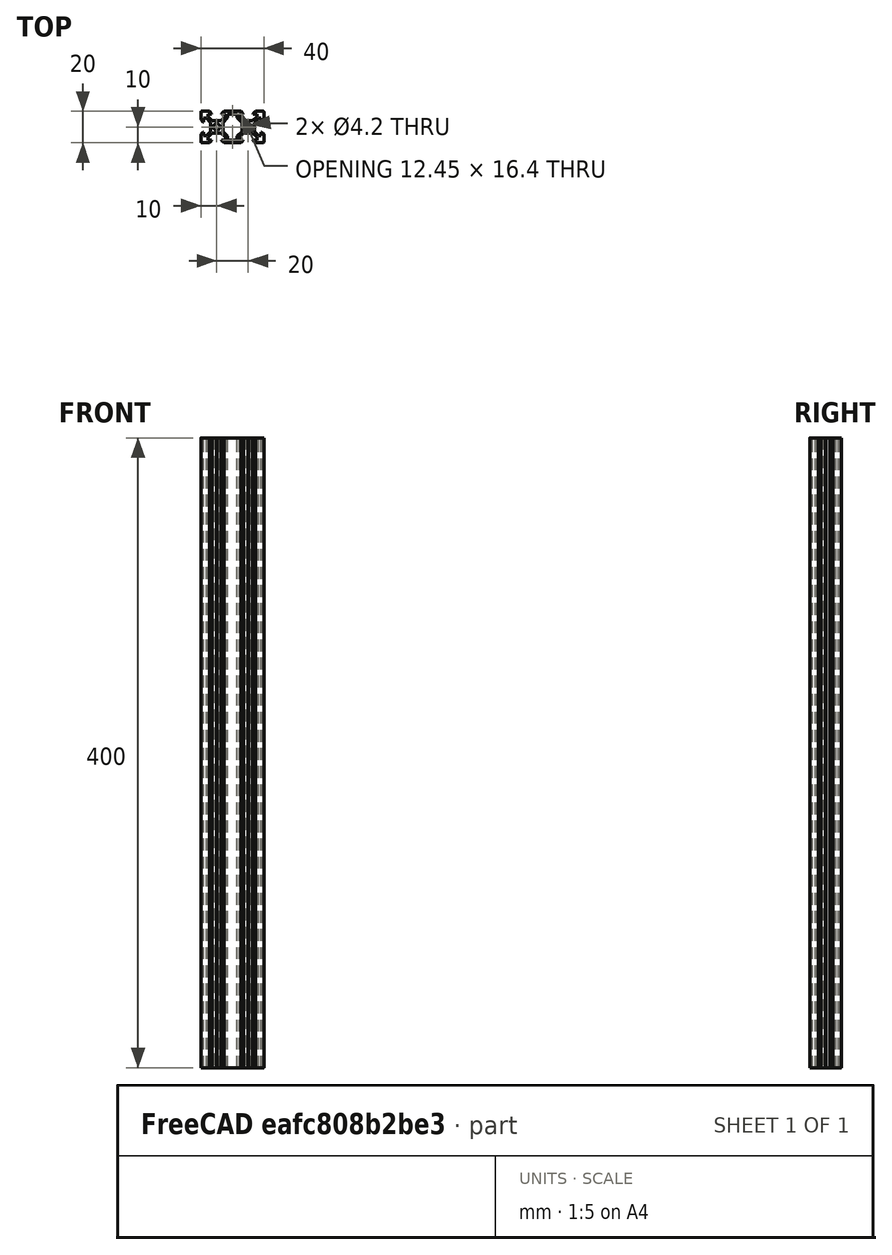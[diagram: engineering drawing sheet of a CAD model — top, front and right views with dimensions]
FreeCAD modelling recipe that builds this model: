
FCSTD DOCUMENT  (FreeCAD 0.20R25566 (Git))
Label: 2040-400
License: All rights reserved
LicenseURL: http://en.wikipedia.org/wiki/All_rights_reserved
objects: Sketcher::SketchObject×1, PartDesign::Pad×1, PartDesign::Body×1
note: 4 computed .brp shape members not serialized (recipe doc carries the construction recipe); baked Part::Feature solids carry a one-line shape summary decoded from their .brp

FEATURE [Sketcher::SketchObject] Sketch
  FullyConstrained = true
  MapMode = 5
  Support = -> [XY_Plane]
  sketch-geometry (114):
    g0: LineSegment StartX=-10 StartY=4.58 StartZ=0 EndX=-10 EndY=9.5 EndZ=0
    g1: LineSegment StartX=-9.5 StartY=10 StartZ=0 EndX=-4.58 EndY=10 EndZ=0
    g2: LineSegment StartX=-5.5 StartY=8.2 StartZ=0 EndX=-3.125 EndY=8.2 EndZ=0
    g3: LineSegment StartX=-8.2 StartY=5.5 StartZ=0 EndX=-8.2 EndY=3.125 EndZ=0
    g4: LineSegment StartX=-0.125 StartY=3.9 StartZ=0 EndX=-2.83934 EndY=3.9 EndZ=0
    g5: LineSegment StartX=-3.9 StartY=2.83934 StartZ=0 EndX=-3.9 EndY=0.125 EndZ=0
    g6: ArcOfCircle CenterX=0 CenterY=3.9 CenterZ=0 NormalX=0 NormalY=0 NormalZ=1 AngleXU=0 Radius=0.125 StartAngle=3.14159 EndAngle=6.28319
    g7: ArcOfCircle CenterX=-3.9 CenterY=0 CenterZ=0 NormalX=0 NormalY=0 NormalZ=1 AngleXU=0 Radius=0.125 StartAngle=4.71239 EndAngle=7.85398
    g8: ArcOfCircle CenterX=-9.5 CenterY=9.5 CenterZ=0 NormalX=0 NormalY=0 NormalZ=1 AngleXU=0 Radius=0.5 StartAngle=1.5708 EndAngle=3.14159
    g9: LineSegment StartX=-5.5 StartY=8.2 StartZ=0 EndX=-5.5 EndY=6.56066 EndZ=0
    g10: LineSegment StartX=-8.2 StartY=5.5 StartZ=0 EndX=-6.56066 EndY=5.5 EndZ=0
    g11: LineSegment StartX=-4.58 StartY=10 StartZ=0 EndX=-3.125 EndY=8.545 EndZ=0
    g12: LineSegment StartX=-3.125 StartY=8.545 StartZ=0 EndX=-3.125 EndY=8.2 EndZ=0
    g13: LineSegment StartX=-10 StartY=4.58 StartZ=0 EndX=-8.545 EndY=3.125 EndZ=0
    g14: LineSegment StartX=-8.545 StartY=3.125 StartZ=0 EndX=-8.2 EndY=3.125 EndZ=0
    g15: LineSegment StartX=-5.5 StartY=6.56066 StartZ=0 EndX=-2.83934 EndY=3.9 EndZ=0
    g16: LineSegment StartX=-6.56066 StartY=5.5 StartZ=0 EndX=-3.9 EndY=2.83934 EndZ=0
    g17: Circle CenterX=0 CenterY=0 CenterZ=0 NormalX=0 NormalY=0 NormalZ=1 AngleXU=0 Radius=2.1
    g18: LineSegment StartX=0.125 StartY=3.9 StartZ=0 EndX=2.83934 EndY=3.9 EndZ=0
    g19: LineSegment StartX=2.83934 StartY=3.9 StartZ=0 EndX=5.5 EndY=6.56066 EndZ=0
    g20: LineSegment StartX=5.5 StartY=6.56066 StartZ=0 EndX=5.5 EndY=8.2 EndZ=0
    g21: LineSegment StartX=3.125 StartY=8.2 StartZ=0 EndX=3.125 EndY=8.545 EndZ=0
    g22: LineSegment StartX=5.5 StartY=8.2 StartZ=0 EndX=3.125 EndY=8.2 EndZ=0
    g23: LineSegment StartX=7 StartY=5.93934 StartZ=0 EndX=3.9 EndY=2.83934 EndZ=0
    g24: LineSegment StartX=3.9 StartY=2.83934 StartZ=0 EndX=3.9 EndY=0.125 EndZ=0
    g25: ArcOfCircle CenterX=3.9 CenterY=0 CenterZ=0 NormalX=0 NormalY=0 NormalZ=1 AngleXU=0 Radius=0.125 StartAngle=1.5708 EndAngle=4.71239
    g26: LineSegment StartX=3.9 StartY=-0.125 StartZ=0 EndX=3.9 EndY=-2.83934 EndZ=0
    g27: LineSegment StartX=3.9 StartY=-2.83934 StartZ=0 EndX=7 EndY=-5.93934 EndZ=0
    g28: LineSegment StartX=4.58 StartY=-10 StartZ=0 EndX=3.125 EndY=-8.545 EndZ=0
    g29: LineSegment StartX=2.83934 StartY=-3.9 StartZ=0 EndX=5.5 EndY=-6.56066 EndZ=0
    g30: LineSegment StartX=3.125 StartY=-8.545 StartZ=0 EndX=3.125 EndY=-8.2 EndZ=0
    g31: LineSegment StartX=3.125 StartY=-8.2 StartZ=0 EndX=5.5 EndY=-8.2 EndZ=0
    g32: LineSegment StartX=5.5 StartY=-8.2 StartZ=0 EndX=5.5 EndY=-6.56066 EndZ=0
    g33: ArcOfCircle CenterX=0 CenterY=-3.9 CenterZ=0 NormalX=0 NormalY=0 NormalZ=1 AngleXU=0 Radius=0.125 StartAngle=0 EndAngle=3.14159
    g34: LineSegment StartX=0.125 StartY=-3.9 StartZ=0 EndX=2.83934 EndY=-3.9 EndZ=0
    g35: LineSegment StartX=-0.125 StartY=-3.9 StartZ=0 EndX=-2.83934 EndY=-3.9 EndZ=0
    g36: LineSegment StartX=-3.9 StartY=-0.125 StartZ=0 EndX=-3.9 EndY=-2.83934 EndZ=0
    g37: LineSegment StartX=-3.9 StartY=-2.83934 StartZ=0 EndX=-6.56066 EndY=-5.5 EndZ=0
    g38: LineSegment StartX=-6.56066 StartY=-5.5 StartZ=0 EndX=-8.2 EndY=-5.5 EndZ=0
    g39: LineSegment StartX=-8.2 StartY=-5.5 StartZ=0 EndX=-8.2 EndY=-3.125 EndZ=0
    g40: LineSegment StartX=-8.2 StartY=-3.125 StartZ=0 EndX=-8.545 EndY=-3.125 EndZ=0
    g41: LineSegment StartX=-8.545 StartY=-3.125 StartZ=0 EndX=-10 EndY=-4.58 EndZ=0
    g42: LineSegment StartX=-10 StartY=-4.58 StartZ=0 EndX=-10 EndY=-9.5 EndZ=0
    g43: ArcOfCircle CenterX=-9.5 CenterY=-9.5 CenterZ=0 NormalX=0 NormalY=0 NormalZ=1 AngleXU=0 Radius=0.5 StartAngle=3.14159 EndAngle=4.71239
    g44: LineSegment StartX=-9.5 StartY=-10 StartZ=0 EndX=-4.58 EndY=-10 EndZ=0
    g45: LineSegment StartX=-4.58 StartY=-10 StartZ=0 EndX=-3.125 EndY=-8.545 EndZ=0
    g46: LineSegment StartX=-2.83934 StartY=-3.9 StartZ=0 EndX=-5.5 EndY=-6.56066 EndZ=0
    g47: LineSegment StartX=-5.5 StartY=-6.56066 StartZ=0 EndX=-5.5 EndY=-8.2 EndZ=0
    g48: LineSegment StartX=-5.5 StartY=-8.2 StartZ=0 EndX=-3.125 EndY=-8.2 EndZ=0
    g49: LineSegment StartX=-3.125 StartY=-8.545 StartZ=0 EndX=-3.125 EndY=-8.2 EndZ=0
    g50: LineSegment StartX=3.125 StartY=8.545 StartZ=0 EndX=4.58 EndY=10 EndZ=0
    g51: LineSegment StartX=-3.9 StartY=2.83934 StartZ=0 EndX=-2.83934 EndY=3.9 EndZ=0
    g52: LineSegment StartX=3.9 StartY=2.83934 StartZ=0 EndX=2.83934 EndY=3.9 EndZ=0
    g53: LineSegment StartX=4.58 StartY=10 StartZ=0 EndX=15.42 EndY=10 EndZ=0
    g54: LineSegment StartX=4.58 StartY=-10 StartZ=0 EndX=15.42 EndY=-10 EndZ=0
    g55: LineSegment StartX=7 StartY=5.93934 StartZ=0 EndX=7 EndY=8.2 EndZ=0
    g56: LineSegment StartX=5.5 StartY=8.2 StartZ=0 EndX=7 EndY=8.2 EndZ=0
    g57: LineSegment StartX=7 StartY=-5.93934 StartZ=0 EndX=7 EndY=-8.2 EndZ=0
    g58: LineSegment StartX=7 StartY=8.2 StartZ=0 EndX=13 EndY=8.2 EndZ=0
    g59: LineSegment StartX=15.42 StartY=10 StartZ=0 EndX=16.875 EndY=8.545 EndZ=0
    g60: LineSegment StartX=16.875 StartY=8.545 StartZ=0 EndX=16.875 EndY=8.2 EndZ=0
    g61: LineSegment StartX=16.875 StartY=8.2 StartZ=0 EndX=14.5 EndY=8.2 EndZ=0
    g62: LineSegment StartX=15.42 StartY=-10 StartZ=0 EndX=16.875 EndY=-8.545 EndZ=0
    g63: LineSegment StartX=16.875 StartY=-8.545 StartZ=0 EndX=16.875 EndY=-8.2 EndZ=0
    g64: LineSegment StartX=16.875 StartY=-8.2 StartZ=0 EndX=14.5 EndY=-8.2 EndZ=0
    g65: LineSegment StartX=7 StartY=-8.2 StartZ=0 EndX=13 EndY=-8.2 EndZ=0
    g66: LineSegment StartX=13 StartY=8.2 StartZ=0 EndX=14.5 EndY=8.2 EndZ=0
    g67: LineSegment StartX=13 StartY=8.2 StartZ=0 EndX=13 EndY=5.93934 EndZ=0
    g68: LineSegment StartX=13 StartY=-8.2 StartZ=0 EndX=13 EndY=-5.93934 EndZ=0
    g69: LineSegment StartX=14.5 StartY=8.2 StartZ=0 EndX=14.5 EndY=6.56066 EndZ=0
    g70: LineSegment StartX=14.5 StartY=-8.2 StartZ=0 EndX=14.5 EndY=-6.56066 EndZ=0
    g71: LineSegment StartX=13 StartY=5.93934 StartZ=0 EndX=16.1 EndY=2.83934 EndZ=0
    g72: LineSegment StartX=14.5 StartY=6.56066 StartZ=0 EndX=17.1607 EndY=3.9 EndZ=0
    g73: LineSegment StartX=13 StartY=-5.93934 StartZ=0 EndX=16.1 EndY=-2.83934 EndZ=0
    g74: LineSegment StartX=14.5 StartY=-6.56066 StartZ=0 EndX=17.1607 EndY=-3.9 EndZ=0
    g75: LineSegment StartX=16.1 StartY=2.83934 StartZ=0 EndX=16.1 EndY=0.125 EndZ=0
    g76: LineSegment StartX=16.1 StartY=-2.83934 StartZ=0 EndX=16.1 EndY=-0.125 EndZ=0
    g77: ArcOfCircle CenterX=16.1 CenterY=0 CenterZ=0 NormalX=0 NormalY=0 NormalZ=1 AngleXU=0 Radius=0.125 StartAngle=4.71239 EndAngle=7.85398
    g78: LineSegment StartX=17.1607 StartY=3.9 StartZ=0 EndX=19.875 EndY=3.9 EndZ=0
    g79: LineSegment StartX=17.1607 StartY=-3.9 StartZ=0 EndX=19.875 EndY=-3.9 EndZ=0
    g80: LineSegment StartX=20.125 StartY=3.9 StartZ=0 EndX=22.8393 EndY=3.9 EndZ=0
    g81: LineSegment StartX=20.125 StartY=-3.9 StartZ=0 EndX=22.8393 EndY=-3.9 EndZ=0
    g82: ArcOfCircle CenterX=20 CenterY=-3.9 CenterZ=0 NormalX=0 NormalY=0 NormalZ=1 AngleXU=0 Radius=0.125 StartAngle=-9e-16 EndAngle=3.14159
    g83: ArcOfCircle CenterX=20 CenterY=3.9 CenterZ=0 NormalX=0 NormalY=0 NormalZ=1 AngleXU=0 Radius=0.125 StartAngle=3.14159 EndAngle=6.28319
    g84: Circle CenterX=20 CenterY=0 CenterZ=0 NormalX=0 NormalY=0 NormalZ=1 AngleXU=0 Radius=2.1
    g85: LineSegment StartX=22.8393 StartY=3.9 StartZ=0 EndX=25.5 EndY=6.56066 EndZ=0
    g86: LineSegment StartX=22.8393 StartY=-3.9 StartZ=0 EndX=25.5 EndY=-6.56066 EndZ=0
    g87: LineSegment StartX=25.5 StartY=6.56066 StartZ=0 EndX=25.5 EndY=8.2 EndZ=0
    g88: LineSegment StartX=25.5 StartY=-6.56066 StartZ=0 EndX=25.5 EndY=-8.2 EndZ=0
    g89: LineSegment StartX=25.5 StartY=8.2 StartZ=0 EndX=23.125 EndY=8.2 EndZ=0
    g90: LineSegment StartX=25.5 StartY=-8.2 StartZ=0 EndX=23.125 EndY=-8.2 EndZ=0
    g91: LineSegment StartX=23.125 StartY=8.2 StartZ=0 EndX=23.125 EndY=8.545 EndZ=0
    g92: LineSegment StartX=23.125 StartY=-8.2 StartZ=0 EndX=23.125 EndY=-8.545 EndZ=0
    g93: LineSegment StartX=23.125 StartY=8.545 StartZ=0 EndX=24.58 EndY=10 EndZ=0
    g94: LineSegment StartX=23.125 StartY=-8.545 StartZ=0 EndX=24.58 EndY=-10 EndZ=0
    g95: LineSegment StartX=24.58 StartY=10 StartZ=0 EndX=29.5 EndY=10 EndZ=0
    g96: LineSegment StartX=24.58 StartY=-10 StartZ=0 EndX=29.5 EndY=-10 EndZ=0
    g97: ArcOfCircle CenterX=29.5 CenterY=9.5 CenterZ=0 NormalX=0 NormalY=0 NormalZ=1 AngleXU=0 Radius=0.5 StartAngle=9e-16 EndAngle=1.5708
    g98: ArcOfCircle CenterX=29.5 CenterY=-9.5 CenterZ=0 NormalX=0 NormalY=0 NormalZ=1 AngleXU=0 Radius=0.5 StartAngle=4.71239 EndAngle=6.28319
    g99: LineSegment StartX=30 StartY=9.5 StartZ=0 EndX=30 EndY=4.58 EndZ=0
    g100: LineSegment StartX=30 StartY=-9.5 StartZ=0 EndX=30 EndY=-4.58 EndZ=0
    g101: LineSegment StartX=30 StartY=-4.58 StartZ=0 EndX=28.545 EndY=-3.125 EndZ=0
    g102: LineSegment StartX=30 StartY=4.58 StartZ=0 EndX=28.545 EndY=3.125 EndZ=0
    g103: LineSegment StartX=28.545 StartY=3.125 StartZ=0 EndX=28.2 EndY=3.125 EndZ=0
    g104: LineSegment StartX=28.545 StartY=-3.125 StartZ=0 EndX=28.2 EndY=-3.125 EndZ=0
    g105: LineSegment StartX=28.2 StartY=3.125 StartZ=0 EndX=28.2 EndY=5.5 EndZ=0
    g106: LineSegment StartX=28.2 StartY=-3.125 StartZ=0 EndX=28.2 EndY=-5.5 EndZ=0
    g107: LineSegment StartX=28.2 StartY=5.5 StartZ=0 EndX=26.5607 EndY=5.5 EndZ=0
    g108: LineSegment StartX=28.2 StartY=-5.5 StartZ=0 EndX=26.5607 EndY=-5.5 EndZ=0
    g109: LineSegment StartX=26.5607 StartY=5.5 StartZ=0 EndX=23.9 EndY=2.83934 EndZ=0
    g110: LineSegment StartX=26.5607 StartY=-5.5 StartZ=0 EndX=23.9 EndY=-2.83934 EndZ=0
    g111: LineSegment StartX=23.9 StartY=2.83934 StartZ=0 EndX=23.9 EndY=0.125 EndZ=0
    g112: LineSegment StartX=23.9 StartY=-2.83934 StartZ=0 EndX=23.9 EndY=-0.125 EndZ=0
    g113: ArcOfCircle CenterX=23.9 CenterY=3.14e-14 CenterZ=0 NormalX=0 NormalY=0 NormalZ=1 AngleXU=0 Radius=0.125 StartAngle=1.5708 EndAngle=4.71236
  constraints (345):
    c: Diameter(g17) = 4.2
    c: Radius(g25) = 0.125
    c: Coincident(g-1,g17)
    c: DistanceY(g43,g1) = 20
    c: Radius(g43) = 0.5
    c: DistanceX(g42,g17) = 10
    c: DistanceY(g43,g17) = 10
    c: Distance(g5,g4) = 1.5
    c: DistanceY(g18,g20) = 4.3
    c: DistanceX(g11,g21) = 6.25
    c: DistanceX(g1,g50) = 9.16
    c: DistanceX(g2,g20) = 11
    c: Coincident(g6,g18)
    c: Coincident(g6,g4)
    c: Coincident(g4,g15)
    c: Coincident(g18,g19)
    c: Coincident(g5,g16)
    c: Coincident(g16,g10)
    c: Coincident(g15,g9)
    c: Coincident(g12,g2)
    c: Coincident(g2,g9)
    c: Coincident(g12,g11)
    c: Coincident(g1,g11)
    c: Coincident(g22,g21)
    c: Coincident(g50,g21)
    c: Coincident(g22,g20)
    c: Coincident(g19,g20)
    c: Coincident(g0,g13)
    c: Coincident(g14,g13)
    c: Coincident(g14,g3)
    c: Coincident(g3,g10)
    c: Coincident(g5,g7)
    c: Coincident(g36,g7)
    c: Coincident(g37,g36)
    c: Coincident(g38,g37)
    c: Coincident(g38,g39)
    c: Coincident(g40,g39)
    c: Coincident(g41,g40)
    c: Coincident(g42,g41)
    c: Coincident(g44,g45)
    c: Coincident(g49,g45)
    c: Coincident(g48,g49)
    c: Coincident(g48,g47)
    c: Coincident(g46,g47)
    c: Coincident(g35,g46)
    c: Coincident(g33,g35)
    c: Coincident(g34,g33)
    c: Coincident(g34,g29)
    c: Coincident(g32,g29)
    c: Coincident(g31,g32)
    c: Coincident(g31,g30)
    c: Coincident(g28,g30)
    c: Coincident(g27,g26)
    c: Coincident(g24,g23)
    c: Coincident(g26,g25)
    c: Coincident(g25,g24)
    c: Vertical(g0)
    c: Horizontal(g1)
    c: Equal(g0,g1)
    c: Horizontal(g4)
    c: PointOnObject(g6,g-2)
    c: Horizontal(g18)
    c: Horizontal(g4,g6)
    c: Horizontal(g6,g6)
    c: Parallel(g13,g11)
    c: Horizontal(g14)
    c: Vertical(g12)
    c: Equal(g14,g12)
    c: Vertical(g3)
    c: Horizontal(g2)
    c: Equal(g3,g2)
    c: Equal(g10,g9)
    c: Horizontal(g10)
    c: Vertical(g9)
    c: Parallel(g16,g15)
    c: Equal(g13,g11)
    c: Tangent(g8,g0) = 1.5708
    c: PointOnObject(g7,g-1)
    c: Vertical(g5)
    c: Vertical(g36)
    c: Vertical(g7,g7)
    c: Vertical(g7,g5)
    c: Horizontal(g38)
    c: Vertical(g39)
    c: Horizontal(g40)
    c: Vertical(g42)
    c: Equal(g36,g5)
    c: Equal(g37,g16)
    c: Perpendicular(g16,g37)
    c: Equal(g38,g10)
    c: Equal(g39,g3)
    c: Equal(g40,g14)
    c: Equal(g41,g13)
    c: Perpendicular(g41,g13)
    c: Equal(g42,g0)
    c: Tangent(g43,g42) = -1.5708
    c: Tangent(g43,g44) = -1.5708
    c: Tangent(g8,g1) = 1.5708
    c: Equal(g43,g8)
    c: Horizontal(g44)
    c: Equal(g44,g42)
    c: Equal(g41,g45)
    c: Parallel(g41,g45)
    c: Vertical(g49)
    c: Equal(g49,g40)
    c: Horizontal(g48)
    c: Vertical(g47)
    c: Equal(g47,g38)
    c: Equal(g46,g37)
    c: Parallel(g46,g37)
    c: PointOnObject(g33,g-2)
    c: Horizontal(g33,g33)
    c: Horizontal(g33,g33)
    c: Horizontal(g35)
    c: Equal(g35,g36)
    c: Horizontal(g34)
    c: Vertical(g32)
    c: Perpendicular(g46,g29)
    c: Equal(g29,g46)
    c: Equal(g32,g47)
    c: Horizontal(g31)
    c: Equal(g31,g48)
    c: Vertical(g30)
    c: Equal(g30,g49)
    c: Perpendicular(g28,g45)
    c: Equal(g28,g45)
    c: Parallel(g29,g27)
    c: PointOnObject(g25,g-1)
    c: Vertical(g26)
    c: Vertical(g25,g24)
    c: Vertical(g24,g25)
    c: Equal(g34,g26)
    c: Equal(g33,g7)
    c: Equal(g7,g6)
    c: Vertical(g24)
    c: Equal(g26,g24)
    c: Equal(g4,g5)
    c: Equal(g4,g18)
    c: Parallel(g23,g19)
    c: Vertical(g20)
    c: Horizontal(g22)
    c: Equal(g22,g2)
    c: Vertical(g21)
    c: Equal(g11,g50)
    c: Horizontal(g2,g21)
    c: Vertical(g10,g37)
    c: Angle(g50,g11) = 1.5708
    c: DistanceY(g2,g1) = 1.8
    c: Equal(g21,g12)
    c: Horizontal(g36,g26)
    c: Vertical(g29,g18)
    c: Coincident(g51,g5)
    c: Coincident(g51,g4)
    c: Coincident(g52,g23)
    c: Coincident(g52,g18)
    c: Equal(g52,g51)
    c: Equal(g15,g19)
    c: Equal(g20,g9)
    c: Horizontal(g53)
    c: Horizontal(g54)
    c: Coincident(g55,g23)
    c: Vertical(g55)
    c: Horizontal(g55,g20)
    c: Coincident(g56,g20)
    c: Coincident(g56,g55)
    c: Equal(g56,g52)
    c: Coincident(g57,g27)
    c: Horizontal(g31,g57)
    c: Vertical(g57)
    c: Vertical(g27,g23)
    c: Coincident(g58,g55)
    c: Horizontal(g58)
    c: Coincident(g59,g53)
    c: Coincident(g60,g59)
    c: Vertical(g60)
    c: Coincident(g61,g60)
    c: Horizontal(g61)
    c: Coincident(g62,g54)
    c: Coincident(g63,g62)
    c: Vertical(g63)
    c: Coincident(g64,g63)
    c: Horizontal(g64)
    c: Coincident(g65,g57)
    c: Horizontal(g65)
    c: Equal(g22,g61)
    c: Equal(g64,g31)
    c: Equal(g59,g50)
    c: Equal(g62,g28)
    c: Equal(g21,g60)
    c: Equal(g30,g63)
    c: Perpendicular(g59,g50)
    c: Perpendicular(g62,g28)
    c: Equal(g58,g65)
    c: Coincident(g66,g58)
    c: Coincident(g66,g61)
    c: Equal(g56,g66)
    c: Coincident(g67,g58)
    c: Vertical(g67)
    c: Coincident(g68,g65)
    c: Vertical(g68)
    c: Coincident(g69,g61)
    c: Vertical(g69)
    c: Coincident(g70,g64)
    c: Vertical(g70)
    c: Equal(g55,g67)
    c: Equal(g57,g68)
    c: Equal(g20,g69)
    c: Equal(g32,g70)
    c: Coincident(g71,g67)
    c: Coincident(g72,g69)
    c: Coincident(g73,g68)
    c: Coincident(g74,g70)
    c: Equal(g23,g71)
    c: Perpendicular(g71,g23)
    c: Equal(g27,g73)
    c: Perpendicular(g73,g27)
    c: Equal(g72,g19)
    c: Perpendicular(g19,g72)
    c: Equal(g74,g29)
    c: Perpendicular(g29,g74)
    c: Coincident(g75,g71)
    c: Vertical(g75)
    c: Coincident(g76,g73)
    c: Vertical(g76)
    c: Equal(g24,g75)
    c: PointOnObject(g77,g-1)
    c: Coincident(g77,g75)
    c: Coincident(g77,g76)
    c: Equal(g25,g77)
    c: Coincident(g78,g72)
    c: Horizontal(g78)
    c: Coincident(g79,g74)
    c: Horizontal(g79)
    c: Equal(g18,g78)
    c: Equal(g34,g79)
    c: Horizontal(g80)
    c: Horizontal(g81)
    c: Equal(g79,g81)
    c: Equal(g78,g80)
    c: Horizontal(g78,g80)
    c: Horizontal(g79,g81)
    c: Coincident(g82,g79)
    c: Coincident(g82,g81)
    c: Coincident(g83,g78)
    c: Coincident(g83,g80)
    c: Equal(g77,g83)
    c: Equal(g77,g82)
    c: Horizontal(g83,g78)
    c: Horizontal(g79,g82)
    c: PointOnObject(g84,g-1)
    c: Equal(g17,g84)
    c: DistanceX(g17,g84) = 20
    c: Vertical(g70,g69)
    c: Coincident(g53,g50)
    c: Coincident(g54,g28)
    c: Vertical(g83,g84)
    c: Coincident(g85,g80)
    c: Coincident(g86,g81)
    c: Equal(g85,g19)
    c: Equal(g86,g29)
    c: Parallel(g19,g85)
    c: Parallel(g86,g29)
    c: Coincident(g87,g85)
    c: Coincident(g88,g86)
    c: Vertical(g88)
    c: Vertical(g87)
    c: Equal(g20,g87)
    c: Equal(g32,g88)
    c: Coincident(g89,g87)
    c: Horizontal(g89)
    c: Coincident(g90,g88)
    c: Horizontal(g90)
    c: Equal(g22,g89)
    c: Equal(g31,g90)
    c: Coincident(g91,g89)
    c: Vertical(g91)
    c: Coincident(g92,g90)
    c: Vertical(g92)
    c: Equal(g21,g91)
    c: Equal(g92,g30)
    c: Coincident(g93,g91)
    c: Coincident(g94,g92)
    c: Coincident(g95,g93)
    c: Horizontal(g95)
    c: Coincident(g96,g94)
    c: Horizontal(g96)
    c: Equal(g50,g93)
    c: Perpendicular(g93,g59)
    c: Equal(g94,g28)
    c: Perpendicular(g94,g62)
    c: Equal(g1,g95)
    c: Equal(g44,g96)
    c: Coincident(g97,g95)
    c: Coincident(g98,g96)
    c: Equal(g8,g97)
    c: Horizontal(g8,g97)
    c: Horizontal(g97,g97)
    c: Horizontal(g98,g43)
    c: Equal(g98,g43)
    c: Horizontal(g98,g98)
    c: Coincident(g99,g97)
    c: Vertical(g99)
    c: Coincident(g100,g98)
    c: Vertical(g100)
    c: Equal(g0,g99)
    c: Equal(g42,g100)
    c: Coincident(g101,g100)
    c: Coincident(g102,g99)
    c: Equal(g101,g41)
    c: Perpendicular(g101,g41)
    c: Equal(g102,g13)
    c: Perpendicular(g13,g102)
    c: Coincident(g103,g102)
    c: Horizontal(g103)
    c: Coincident(g104,g101)
    c: Horizontal(g104)
    c: Equal(g103,g14)
    c: Equal(g104,g40)
    c: Coincident(g105,g103)
    c: Vertical(g105)
    c: Coincident(g106,g104)
    c: Vertical(g106)
    c: Equal(g3,g105)
    c: Equal(g106,g39)
    c: Coincident(g107,g105)
    c: Horizontal(g107)
    c: Coincident(g108,g106)
    c: Horizontal(g108)
    c: Equal(g38,g108)
    c: Equal(g10,g107)
    c: Coincident(g109,g107)
    c: Coincident(g110,g108)
    c: Equal(g110,g37)
    c: Perpendicular(g37,g110)
    c: Equal(g109,g16)
    c: Perpendicular(g16,g109)
    c: Coincident(g111,g109)
    c: Vertical(g111)
    c: Coincident(g112,g110)
    c: Vertical(g112)
    c: Equal(g76,g112)
    c: Equal(g75,g111)
    c: Coincident(g113,g111)
    c: Coincident(g113,g112)
    c: Vertical(g113,g111)
FEATURE [PartDesign::Pad] Pad
  Direction = (0,0,1)
  Length = 400
  Length2 = 100
  Profile = -> Sketch
  Type = 0
FEATURE [PartDesign::Body] Body  label="2020-400"
  Group = -> [Sketch,Pad]
  Origin = -> Origin
  Tip = -> Pad
